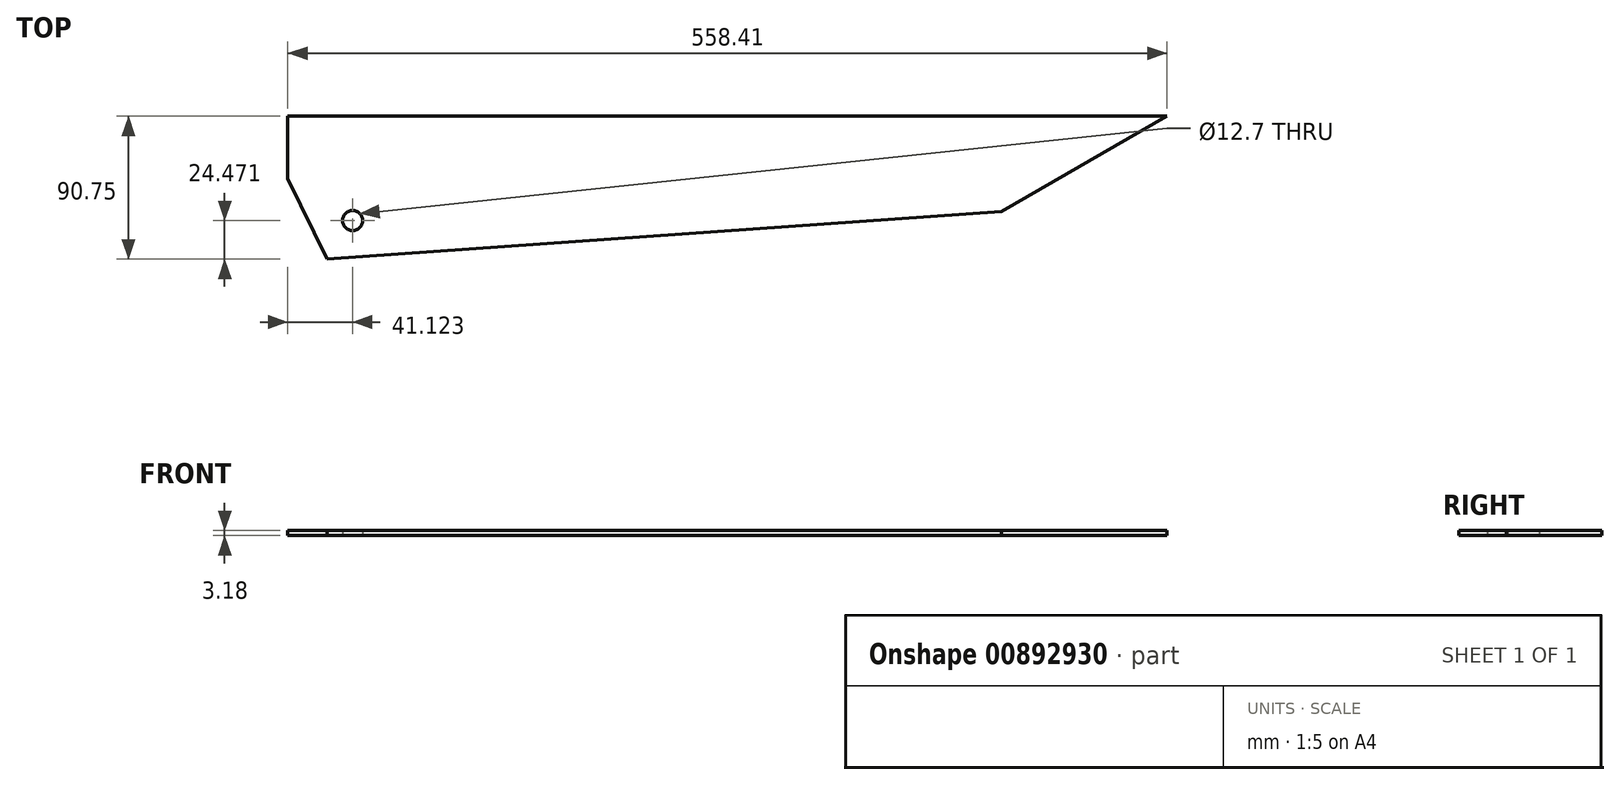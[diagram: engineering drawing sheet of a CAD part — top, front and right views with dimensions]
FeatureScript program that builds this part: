
annotation { "Feature Type Name" : "Feature", "Feature Type Description" : "" }
export const myFeature = defineFeature(function(context is Context, id is Id, definition is map)
    precondition{}
    {
        {
            var Q0;
            Q0=qCreatedBy(makeId("Top.planeOp"),FACE);
            var sketch = newSketch(context, id + "F0", { "sketchPlane" : qUnion([Q0])});
            skLineSegment(sketch, "E0", {"start": v(284.07, 274.7) * mm, "end": v(284.07, -690.5) * mm, "construction": true});
            skLineSegment(sketch, "E1", {"start": v(284.07, -690.5) * mm, "end": v(195.17, -690.5) * mm, "construction": true});
            skLineSegment(sketch, "E2", {"start": v(-249.48, 223.63) * mm, "end": v(195.17, -690.5) * mm, "construction": true});
            skLineSegment(sketch, "E3", {"start": v(-274.34, 274.7) * mm, "end": v(-274.34, 314.38) * mm});
            skCircle(sketch, "E4", {"center": v(-233.22, 248.1) * mm, "radius": 22.23 * mm});
            skLineSegment(sketch, "E5.0", {"start": v(284.07, 314.38) * mm, "end": v(-274.34, 314.38) * mm});
            skLineSegment(sketch, "E6", {"start": v(-274.34, 274.7) * mm, "end": v(-249.48, 223.63) * mm});
            skLineSegment(sketch, "E7", {"start": v(-274.34, 274.7) * mm, "end": v(215.33, 274.7) * mm});
            skLineSegment(sketch, "E8", {"start": v(284.07, 314.38) * mm, "end": v(284.07, 274.7) * mm});
            skLineSegment(sketch, "E9", {"start": v(-249.48, 223.63) * mm, "end": v(179, 253.73) * mm});
            skCircle(sketch, "E10", {"center": v(-233.22, 248.1) * mm, "radius": 6.35 * mm});
            skLineSegment(sketch, "E11", {"start": v(284.07, 314.38) * mm, "end": v(179, 253.73) * mm});
            skLineSegment(sketch, "E12", {"start": v(-233.07, 305.97) * mm, "end": v(-194.85, 227.47) * mm});
            skLineSegment(sketch, "E13", {"start": v(-233.07, 305.97) * mm, "end": v(-233.07, 314.38) * mm});
            skSolve(sketch);
        }
        {
            var Q0;
            {var subQ0=sQuery(id+"F0.wireOp",EDGE,"5278pz5J-vCxS-k4Ku-7Duq-7MSw0lDqNbda");Q0=makeQuery(id+"F0.imprint","IMPRINT",FACE,{"disambiguationData":[TD([[makeQuery(id+"F0.imprint","IMPRINT",EDGE,{"derivedFrom":subQ0}),-1.0]])]});}
            var Q1;
            Q1=makeQuery(id+"F0.imprint","IMPRINT",FACE,{"disambiguationData":[TD([[makeQuery(id+"F0.imprint","IMPRINT",EDGE,{"derivedFrom":sQuery(id+"F0.wireOp",EDGE,"E4")}),-1.0]])]});
            var Q2;
            Q2=makeQuery(id+"F0.imprint","IMPRINT",FACE,{"disambiguationData":[TD([[makeQuery(id+"F0.imprint","IMPRINT",EDGE,{"derivedFrom":sQuery(id+"F0.wireOp",EDGE,"E4")}),1.0]])]});
            var Q3;
            {var subQ1=sQuery(id+"F0.wireOp",EDGE,"E3");Q3=makeQuery(id+"F0.imprint","IMPRINT",FACE,{"disambiguationData":[TD([[makeQuery(id+"F0.imprint","IMPRINT",EDGE,{"derivedFrom":subQ1}),-1.0]])]});}
            var Q4;
            {var subQ3=sQuery(id+"F0.wireOp",EDGE,"34cbd23b-e941-41b4-9f00-e5173009a71e.0");Q4=makeQuery(id+"F0.imprint","IMPRINT",FACE,{"disambiguationData":[TD([[makeQuery(id+"F0.imprint","IMPRINT",EDGE,{"derivedFrom":subQ3}),1.0]])]});}
            var Q5;
            {var subQ2=sQuery(id+"F0.wireOp",EDGE,"f16659ca-f6a7-4245-8b89-f26018f7c24f.0");Q5=makeQuery(id+"F0.imprint","IMPRINT",FACE,{"disambiguationData":[TD([[makeQuery(id+"F0.imprint","IMPRINT",EDGE,{"derivedFrom":subQ2}),-1.0]])]});}
            var Q6;
            {var subQ0=sQuery(id+"F0.wireOp",EDGE,"E11");var subQ1=sQuery(id+"F0.wireOp",EDGE,"E5.0");var subQ2=makeQuery(id+"F0.imprint","INTERSECT",VERTEX,{"derivedFrom":[subQ1,subQ0]});Q6=makeQuery(id+"F0.imprint","IMPRINT",FACE,{"disambiguationData":[TD([[makeQuery(id+"F0.imprint","IMPRINT",EDGE,{"disambiguationData":[TD([[subQ2,-1.0]])],"derivedFrom":subQ1}),1.0]])]});}
            var Q7;
            {var subQ0=sQuery(id+"F0.wireOp",EDGE,"34cbd23b-e941-41b4-9f00-e5173009a71e.0");var subQ1=sQuery(id+"F0.wireOp",EDGE,"E7");var subQ2=makeQuery(id+"F0.imprint","INTERSECT",VERTEX,{"derivedFrom":[subQ1,subQ0]});Q7=makeQuery(id+"F0.imprint","IMPRINT",FACE,{"disambiguationData":[TD([[makeQuery(id+"F0.imprint","IMPRINT",EDGE,{"disambiguationData":[TD([[subQ2,1.0]])],"derivedFrom":subQ1}),-1.0]])]});}
            var Q8;
            {var subQ1=sQuery(id+"F0.wireOp",EDGE,"E7");var subQ5=sQuery(id+"F0.wireOp",EDGE,"E11");var subQ6=makeQuery(id+"F0.imprint","INTERSECT",VERTEX,{"derivedFrom":[subQ1,subQ5]});Q8=makeQuery(id+"F0.imprint","IMPRINT",FACE,{"disambiguationData":[TD([[makeQuery(id+"F0.imprint","IMPRINT",EDGE,{"disambiguationData":[TD([[subQ6,1.0]])],"derivedFrom":subQ1}),-1.0]])]});}
            extrude(context, id + "F1", {"entities" : qUnion([Q0, Q1, Q2, Q3, Q4, Q5, Q6, Q7, Q8]), "depth" : 3.17 * mm, "offsetDistance" : 25.4 * mm});
        }
    });
